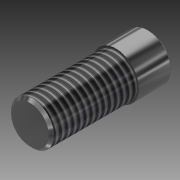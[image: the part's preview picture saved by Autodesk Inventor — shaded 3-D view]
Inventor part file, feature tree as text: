
AUTODESK INVENTOR PART (.ipt)
format: ipt  version: 2014 SP1 (Build 180222100, 222)  size: 113,664 bytes
history: native  units: mm (DEFAULTED — no unit token found)
features: extrude x2, chamfer x2, sketch x2, thread x1, reference x1
ambient origin geometry x8: Origin, YZ Plane, XZ Plane, XY Plane, X Axis, Y Axis, Z Axis, Center Point
bodies: Solid1 (feature_tree)
feature tree (8):
  extrude  "Extrusion1"  Depth=5.08mm TaperAngle=0.0deg
  chamfer  "Chamfer1"  Distance=3.175mm
  extrude  "Extrusion2"  Depth=12.7mm TaperAngle=0.0deg
  chamfer  "Chamfer2"  Distance=3.175mm
  thread  "Thread1"  [1 undecoded]
  sketch  "Sketch1"  dims[d0=6.858mm d1=5.08mm d2=0.0mm d3=0.381mm d4=3.175mm]
  reference  "Reference1"
  sketch  "Sketch2"  dims[d5=6.35mm d6=12.7mm d7=0.0mm d8=0.381mm d9=3.175mm d10=25.4mm d11=0.0mm d12=45.0deg d13=45.0deg]
note: 1 required parameter value undecoded (feature->parameter linkage not recoverable at this tier; creation-order binding heuristic only, values carry confidence <= 0.55)
